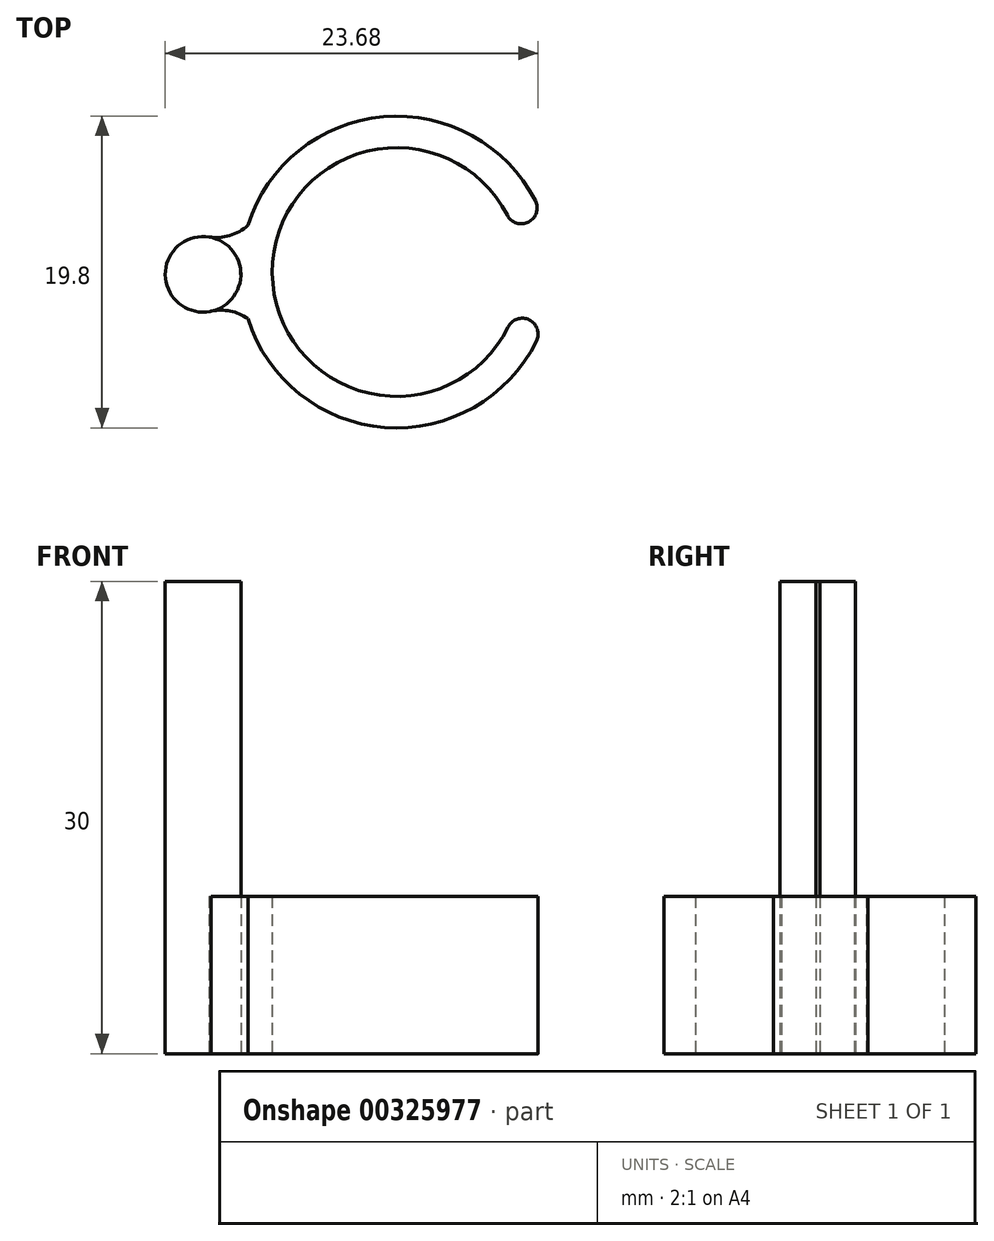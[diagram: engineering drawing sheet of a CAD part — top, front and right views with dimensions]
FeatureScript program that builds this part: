
annotation { "Feature Type Name" : "Feature", "Feature Type Description" : "" }
export const myFeature = defineFeature(function(context is Context, id is Id, definition is map)
    precondition{}
    {
        {
            var Q0;
            Q0=qCreatedBy(makeId("Top.planeOp"),FACE);
            var sketch = newSketch(context, id + "F0", { "sketchPlane" : qUnion([Q0])});
            skCircle(sketch, "E0", {"center": v(-12.3, -0.15) * mm, "radius": 2.4 * mm});
            skPoint(sketch, "E0.first.point", {"position": v(-9.9, 0) * mm});
            skPoint(sketch, "E0.second.point", {"position": v(-14.7, 0) * mm});
            skPoint(sketch, "E0.third.point", {"position": v(-11.8, -2.5) * mm});
            skArc(sketch, "E1", {"start": v(9.37, 3.2) * mm, "mid": v(-9.9, -0.22) * mm, "end": v(9.5, -2.78) * mm});
            skArc(sketch, "E2.0", {"start": v(7.3, 3) * mm, "mid": v(-7.9, 0) * mm, "end": v(7.3, -3) * mm});
            skLineSegment(sketch, "E3", {"start": v(7.3, 3) * mm, "end": v(9.37, 3.2) * mm});
            skLineSegment(sketch, "E4", {"start": v(7.3, -3) * mm, "end": v(9.5, -2.78) * mm});
            skArc(sketch, "E5", {"start": v(-9.45, -2.97) * mm, "mid": v(-10.57, -2.49) * mm, "end": v(-11.8, -2.5) * mm});
            skArc(sketch, "E6", {"start": v(-11.92, 2.22) * mm, "mid": v(-10.6, 2.31) * mm, "end": v(-9.45, 2.97) * mm});
            skSolve(sketch);
        }
        {
            var Q0;
            Q0=makeQuery(id+"F0.imprint","IMPRINT",FACE,{"disambiguationData":[TD([[makeQuery(id+"F0.imprint","IMPRINT",EDGE,{"derivedFrom":sQuery(id+"F0.wireOp",EDGE,"E2.0")}),-1.0]])]});
            var Q1;
            {var subQ0=sQuery(id+"F0.wireOp",EDGE,"E6");Q1=makeQuery(id+"F0.imprint","IMPRINT",FACE,{"disambiguationData":[TD([[makeQuery(id+"F0.imprint","IMPRINT",EDGE,{"derivedFrom":subQ0}),-1.0]])]});}
            var Q2;
            {var subQ0=sQuery(id+"F0.wireOp",EDGE,"E5");Q2=makeQuery(id+"F0.imprint","IMPRINT",FACE,{"disambiguationData":[TD([[makeQuery(id+"F0.imprint","IMPRINT",EDGE,{"derivedFrom":subQ0}),-1.0]])]});}
            extrude(context, id + "F1", {"entities" : qUnion([Q0, Q1, Q2]), "depth" : 10 * mm});
        }
        {
            var Q0;
            {var subQ0=sQuery(id+"F0.wireOp",EDGE,"E1");var subQ1=sQuery(id+"F0.wireOp",EDGE,"E0");var subQ2=makeQuery(id+"F0.imprint","INTERSECT",VERTEX,{"disambiguationData":[OD(0.0)],"derivedFrom":[subQ1,subQ0]});Q0=makeQuery(id+"F0.imprint","IMPRINT",FACE,{"disambiguationData":[TD([[makeQuery(id+"F0.imprint","IMPRINT",EDGE,{"disambiguationData":[TD([[subQ2,-1.0]])],"derivedFrom":subQ1}),1.0]])]});}
            extrude(context, id + "F2", {"entities" : qUnion([Q0]), "depth" : 30 * mm});
        }
        {
            var Q0;
            Q0=makeQuery(id+"F1.opExtrude","SWEPT_EDGE",EDGE,{"disambiguationData":[OSD([sQuery(id+"F0.wireOp",EDGE,"E1"),sQuery(id+"F0.wireOp",EDGE,"E4")])]});
            var Q1;
            Q1=makeQuery(id+"F1.opExtrude","SWEPT_EDGE",EDGE,{"disambiguationData":[OSD([sQuery(id+"F0.wireOp",EDGE,"E2.0"),sQuery(id+"F0.wireOp",EDGE,"E4")])]});
            var Q2;
            Q2=makeQuery(id+"F1.opExtrude","SWEPT_EDGE",EDGE,{"disambiguationData":[OSD([sQuery(id+"F0.wireOp",EDGE,"E1"),sQuery(id+"F0.wireOp",EDGE,"E3")])]});
            var Q3;
            Q3=makeQuery(id+"F1.opExtrude","SWEPT_EDGE",EDGE,{"disambiguationData":[OSD([sQuery(id+"F0.wireOp",EDGE,"E2.0"),sQuery(id+"F0.wireOp",EDGE,"E3")])]});
            fillet(context, id + "F3", {"entities" : qUnion([Q0, Q1, Q2, Q3]), "radius" : 1 * mm, "tangentPropagation" : true, "allowEdgeOverflow" : false});
        }
    });
